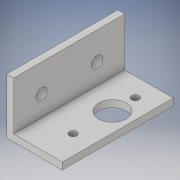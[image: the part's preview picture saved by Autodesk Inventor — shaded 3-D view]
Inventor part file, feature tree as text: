
AUTODESK INVENTOR PART (.ipt)
format: ipt  version: 2018 (Build 220112000, 112)  size: 135,680 bytes
history: native  units: in
note: dims shown in document units (in); Inventor stores cm internally (conversion verified against a paired STEP export)
features: extrude x4, sketch x3
ambient origin geometry x8: Origin, YZ Plane, XZ Plane, XY Plane, X Axis, Y Axis, Z Axis, Center Point
bodies: Solid1 (feature_tree)
feature tree (7):
  extrude  "Extrusion1"  Depth=1.0in
  extrude  "Extrusion2"  Depth=0.125in
  extrude  "Extrusion3"  Depth=1.0in
  extrude  "Extrusion4"  Depth=1.0in
  sketch  "Sketch1"  dims[d0=0.125in d1=1.0in]
  sketch  "Sketch3"  dims[d2=1.0in d3=0.125in]
  sketch  "Sketch4"  dims[d4=2.0in d5=0.0in d6=0.655in d9=0.5in d10=2.0in d11=0.0in d12=0.75in d13=0.413in d14=1.122in d15=0.134in d16=1.0in d17=0.0in d18=0.5in d19=0.5in d20=1.0in d21=0.2031in d22=1.0in d23=0.0in]
